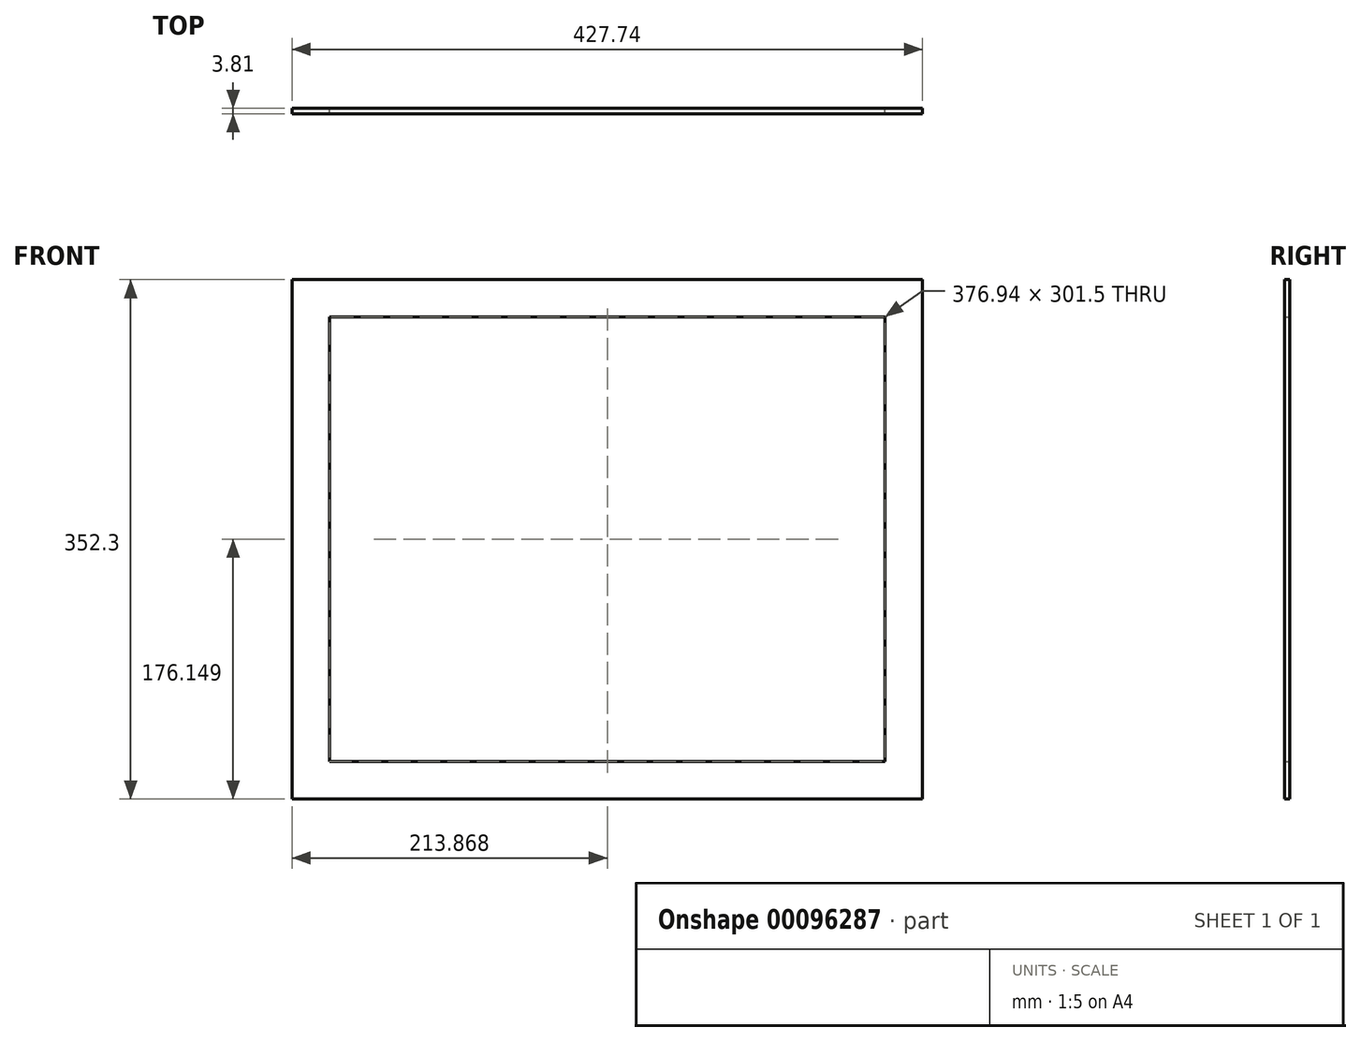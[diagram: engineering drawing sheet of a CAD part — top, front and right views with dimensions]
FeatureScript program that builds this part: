
annotation { "Feature Type Name" : "Feature", "Feature Type Description" : "" }
export const myFeature = defineFeature(function(context is Context, id is Id, definition is map)
    precondition{}
    {
        {
            var Q0;
            Q0=qCreatedBy(makeId("Front.planeOp"),FACE);
            var sketch = newSketch(context, id + "F0", { "sketchPlane" : qUnion([Q0])});
            skLineSegment(sketch, "E0", {"start": v(0, 0) * mm, "end": v(376.94, 0) * mm});
            skLineSegment(sketch, "E1", {"start": v(376.94, 0) * mm, "end": v(376.94, 301.5) * mm});
            skLineSegment(sketch, "E2", {"start": v(0, 0) * mm, "end": v(0, 301.5) * mm});
            skLineSegment(sketch, "E3", {"start": v(0, 301.5) * mm, "end": v(376.94, 301.5) * mm});
            skLineSegment(sketch, "E4", {"start": v(-25.4, 326.9) * mm, "end": v(402.34, 326.9) * mm});
            skLineSegment(sketch, "E5", {"start": v(402.34, 326.9) * mm, "end": v(402.34, -25.4) * mm});
            skLineSegment(sketch, "E6", {"start": v(402.34, -25.4) * mm, "end": v(-25.4, -25.4) * mm});
            skLineSegment(sketch, "E7", {"start": v(-25.4, 326.9) * mm, "end": v(-25.4, -25.4) * mm});
            skSolve(sketch);
        }
        {
            var Q0;
            Q0=makeQuery(id+"F0.imprint","IMPRINT",FACE,{"disambiguationData":[TD([[makeQuery(id+"F0.imprint","IMPRINT",EDGE,{"derivedFrom":sQuery(id+"F0.wireOp",EDGE,"E0")}),-1.0]])]});
            extrude(context, id + "F1", {"entities" : qUnion([Q0]), "depth" : 3.8 * mm});
        }
    });
